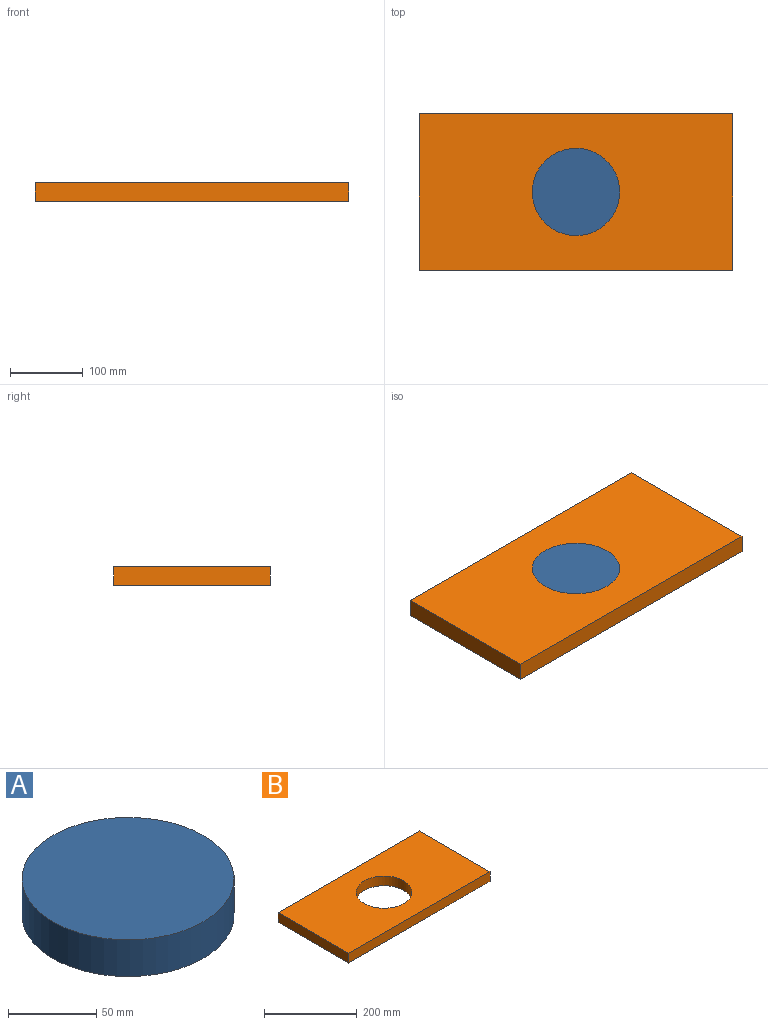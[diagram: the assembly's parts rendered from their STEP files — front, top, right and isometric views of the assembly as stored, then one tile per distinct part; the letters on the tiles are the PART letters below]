
ASSEMBLY  parts=2 mates=1
PART A: 3 faces, bbox 120x120x25.4 mm
  f0: cylinder r=60mm len=120mm, axis (0,0,-1), area 9575.6mm2, adj f1,f2
  f1: plane 120x120mm, normal (0,0,1), area 11309.7mm2, adj f0
  f2: plane 120x120mm, normal (0,0,-1), area 11309.7mm2, adj f0
PART B: 7 faces, bbox 430x215x25.4 mm
  f0: plane 430x25.4mm, normal (0,-1,0), area 10922mm2, adj f1,f3,f5,f6
  f1: plane 215x25.4mm, normal (1,0,0), area 5461mm2, adj f0,f2,f5,f6
  f2: plane 430x25.4mm, normal (0,1,0), area 10922mm2, adj f1,f3,f5,f6
  f3: plane 215x25.4mm, normal (-1,0,0), area 5461mm2, adj f0,f2,f5,f6
  f4: cylinder r=60mm len=120mm, axis (0,0,-1), area 9575.6mm2, adj f5,f6
  f5: plane 430x215mm, normal (0,0,1), area 81140.3mm2, adj f0,f1,f2,f3,f4
  f6: plane 430x215mm, normal (0,0,-1), area 81140.3mm2, adj f0,f1,f2,f3,f4
PLACE A t=(-484.83,-422.76,105.2)mm
PLACE B t=(-13.94,-161.08,105.2)mm
MATE fastened A.f0 <-> B.f4  axis (0,0,-1) through (-228.94,-53.58,117.9)mm
